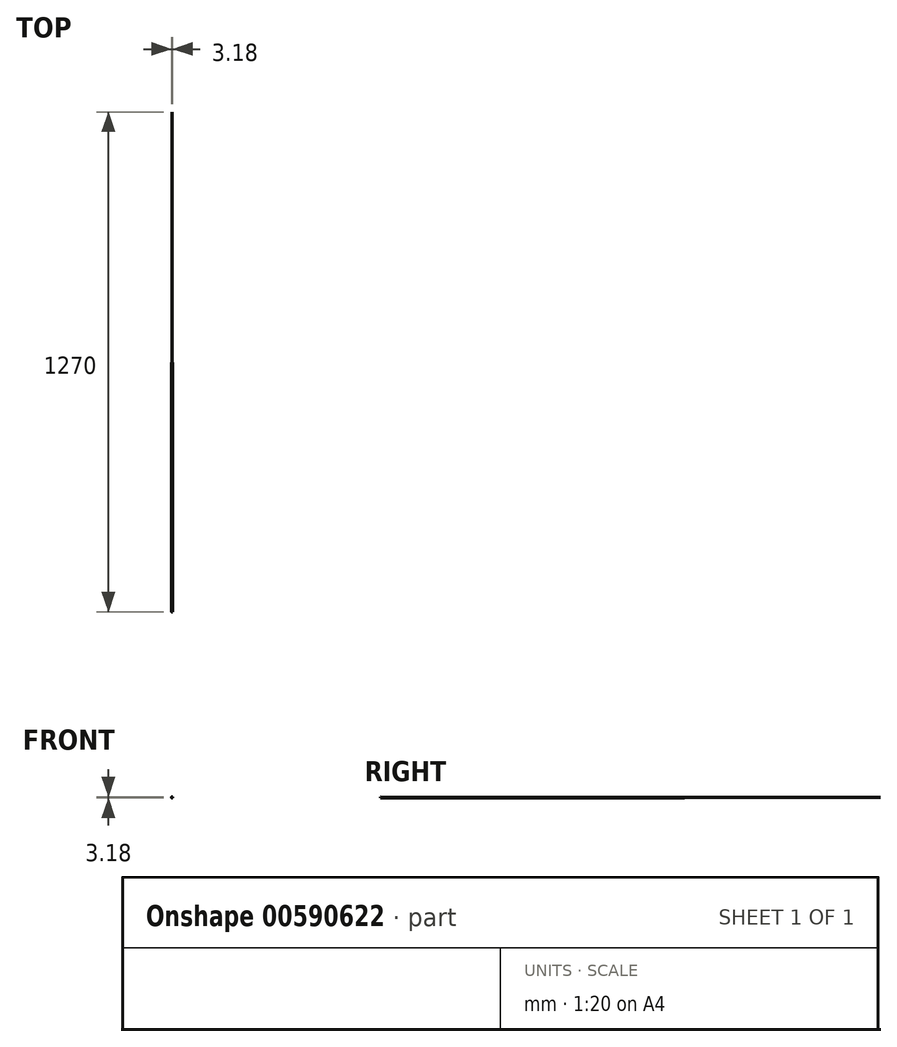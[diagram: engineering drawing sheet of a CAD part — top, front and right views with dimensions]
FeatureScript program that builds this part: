
annotation { "Feature Type Name" : "Feature", "Feature Type Description" : "" }
export const myFeature = defineFeature(function(context is Context, id is Id, definition is map)
    precondition{}
    {
        {
            var Q0;
            Q0=qCreatedBy(makeId("Front.planeOp"),FACE);
            cPlane(context, id + "F0", {"entities" : qUnion([Q0]), "cplaneType" : CPlaneType.OFFSET, "offset" : 635 * mm, "width" : 152.4 * mm, "height" : 152.4 * mm});
        }
        {
            var Q0;
            Q0=qCreatedBy(makeId("Front.planeOp"),FACE);
            cPlane(context, id + "F1", {"entities" : qUnion([Q0]), "cplaneType" : CPlaneType.OFFSET, "offset" : 635 * mm, "oppositeDirection" : true, "width" : 152.4 * mm, "height" : 152.4 * mm});
        }
        {
            var Q0;
            Q0=qCreatedBy(id+"F0.planeOp",FACE);
            var sketch = newSketch(context, id + "F2", { "sketchPlane" : qUnion([Q0])});
            skCircle(sketch, "E0", {"center": v(0, 0) * mm, "radius": 1.59 * mm});
            skSolve(sketch);
        }
        {
            var Q0;
            Q0=qCreatedBy(id+"F1.planeOp",FACE);
            var sketch = newSketch(context, id + "F3", { "sketchPlane" : qUnion([Q0])});
            skCircle(sketch, "E1", {"center": v(0, 0) * mm, "radius": 0 * mm});
            skSolve(sketch);
        }
        {
            var Q0;
            Q0=makeQuery(id+"F3.imprint","IMPRINT",FACE,{"disambiguationData":[TD([[makeQuery(id+"F3.imprint","IMPRINT",EDGE,{"derivedFrom":sQuery(id+"F3.wireOp",EDGE,"E1")}),1.0]])]});
            var Q1;
            Q1=makeQuery(id+"F2.imprint","IMPRINT",FACE,{"disambiguationData":[TD([[makeQuery(id+"F2.imprint","IMPRINT",EDGE,{"derivedFrom":sQuery(id+"F2.wireOp",EDGE,"E0")}),1.0]])]});
            loft(context, id + "F4", {"sheetProfilesArray" : [{ "sheetProfileEntities" : qUnion([Q0]) }, { "sheetProfileEntities" : qUnion([Q1]) }]});
        }
    });
